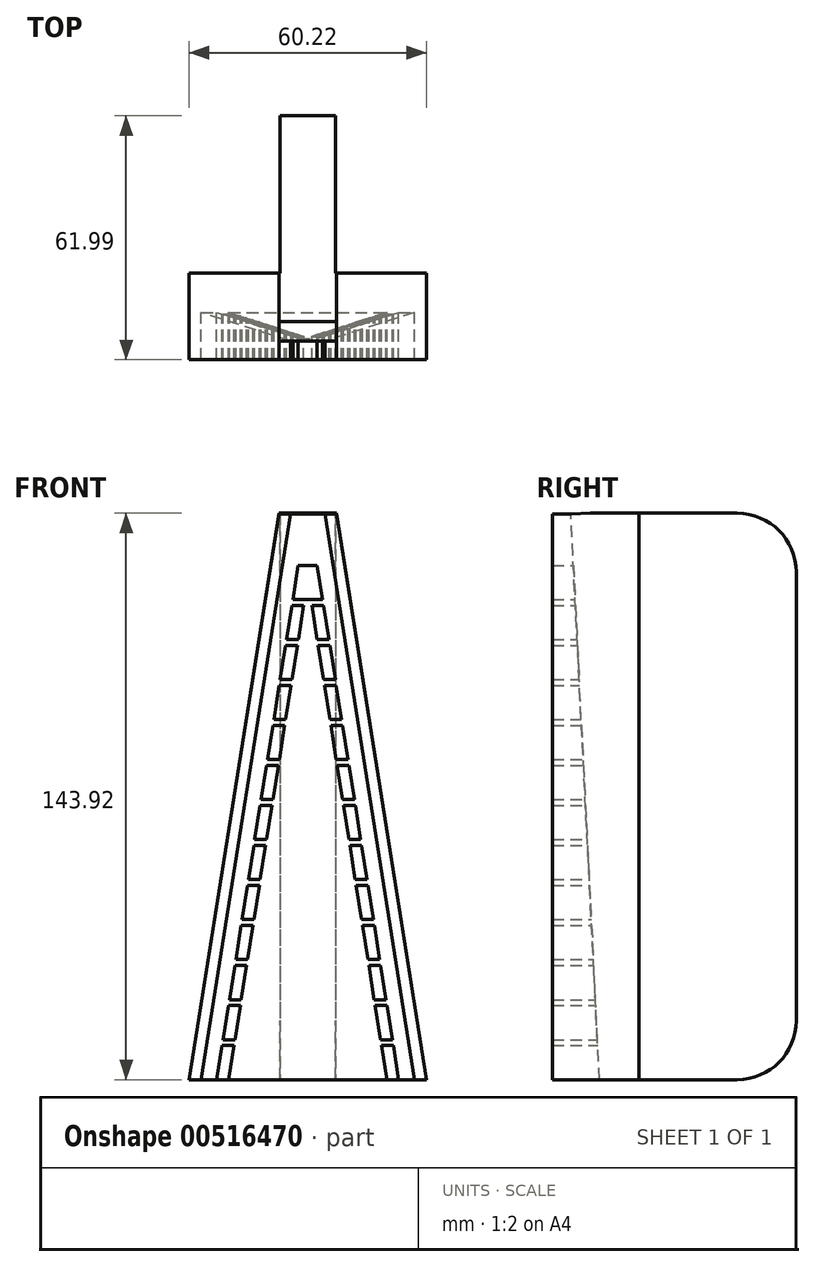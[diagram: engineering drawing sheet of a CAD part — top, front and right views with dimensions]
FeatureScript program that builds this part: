
annotation { "Feature Type Name" : "Feature", "Feature Type Description" : "" }
export const myFeature = defineFeature(function(context is Context, id is Id, definition is map)
    precondition{}
    {
        {
            var Q0;
            Q0=qCreatedBy(makeId("Front.planeOp"),FACE);
            var sketch = newSketch(context, id + "F0", { "sketchPlane" : qUnion([Q0])});
            skLineSegment(sketch, "E0", {"start": v(-21.74, 8.67) * mm, "end": v(-18.74, 8.67) * mm});
            skLineSegment(sketch, "E1", {"start": v(-18.74, 8.67) * mm, "end": v(-20.11, 0) * mm});
            skLineSegment(sketch, "E2", {"start": v(-20.11, 0) * mm, "end": v(-23.11, 0) * mm});
            skLineSegment(sketch, "E3", {"start": v(-23.11, 0) * mm, "end": v(-21.74, 8.67) * mm});
            skLineSegment(sketch, "E4", {"start": v(18.74, 8.67) * mm, "end": v(21.74, 8.67) * mm});
            skLineSegment(sketch, "E5", {"start": v(21.74, 8.67) * mm, "end": v(23.11, 0) * mm});
            skLineSegment(sketch, "E6", {"start": v(23.11, 0) * mm, "end": v(20.11, 0) * mm});
            skLineSegment(sketch, "E7", {"start": v(20.11, 0) * mm, "end": v(18.74, 8.67) * mm});
            skLineSegment(sketch, "E8", {"start": v(-21.5, 10.17) * mm, "end": v(-18.5, 10.17) * mm});
            skLineSegment(sketch, "E9", {"start": v(-18.5, 10.17) * mm, "end": v(-17.13, 18.83) * mm});
            skLineSegment(sketch, "E10", {"start": v(-17.13, 18.83) * mm, "end": v(-20.13, 18.83) * mm});
            skLineSegment(sketch, "E11", {"start": v(-20.13, 18.83) * mm, "end": v(-21.5, 10.17) * mm});
            skLineSegment(sketch, "E12", {"start": v(18.5, 10.17) * mm, "end": v(17.13, 18.83) * mm});
            skLineSegment(sketch, "E13", {"start": v(17.13, 18.83) * mm, "end": v(20.13, 18.83) * mm});
            skLineSegment(sketch, "E14", {"start": v(20.13, 18.83) * mm, "end": v(21.5, 10.17) * mm});
            skLineSegment(sketch, "E15", {"start": v(21.5, 10.17) * mm, "end": v(18.5, 10.17) * mm});
            skLineSegment(sketch, "E16", {"start": v(-18.52, 29) * mm, "end": v(-19.89, 20.33) * mm});
            skLineSegment(sketch, "E17", {"start": v(-19.89, 20.33) * mm, "end": v(-16.89, 20.33) * mm});
            skLineSegment(sketch, "E18", {"start": v(-16.89, 20.33) * mm, "end": v(-15.52, 29) * mm});
            skLineSegment(sketch, "E19", {"start": v(-15.52, 29) * mm, "end": v(-18.52, 29) * mm});
            skLineSegment(sketch, "E20", {"start": v(19.89, 20.33) * mm, "end": v(18.52, 29) * mm});
            skLineSegment(sketch, "E21", {"start": v(18.52, 29) * mm, "end": v(15.52, 29) * mm});
            skLineSegment(sketch, "E22", {"start": v(15.52, 29) * mm, "end": v(16.89, 20.33) * mm});
            skLineSegment(sketch, "E23", {"start": v(16.89, 20.33) * mm, "end": v(19.89, 20.33) * mm});
            skLineSegment(sketch, "E24", {"start": v(-16.67, 40.67) * mm, "end": v(-13.67, 40.67) * mm});
            skLineSegment(sketch, "E25", {"start": v(-13.67, 40.67) * mm, "end": v(-12.3, 49.33) * mm});
            skLineSegment(sketch, "E26", {"start": v(-12.3, 49.33) * mm, "end": v(-15.3, 49.33) * mm});
            skLineSegment(sketch, "E27", {"start": v(-15.3, 49.33) * mm, "end": v(-16.67, 40.67) * mm});
            skLineSegment(sketch, "E28", {"start": v(-13.69, 59.5) * mm, "end": v(-15.06, 50.83) * mm});
            skLineSegment(sketch, "E29", {"start": v(-8.84, 71.17) * mm, "end": v(-11.84, 71.17) * mm});
            skLineSegment(sketch, "E30", {"start": v(-7.47, 79.83) * mm, "end": v(-10.47, 79.83) * mm});
            skLineSegment(sketch, "E31", {"start": v(-10.47, 79.83) * mm, "end": v(-11.84, 71.17) * mm});
            skLineSegment(sketch, "E32", {"start": v(-8.86, 90) * mm, "end": v(-10.23, 81.33) * mm});
            skLineSegment(sketch, "E33", {"start": v(-10.23, 81.33) * mm, "end": v(-7.23, 81.33) * mm});
            skLineSegment(sketch, "E34", {"start": v(-7.23, 81.33) * mm, "end": v(-5.86, 90) * mm});
            skLineSegment(sketch, "E35", {"start": v(-5.86, 90) * mm, "end": v(-8.86, 90) * mm});
            skLineSegment(sketch, "E36", {"start": v(-7.25, 100.17) * mm, "end": v(-8.62, 91.5) * mm});
            skLineSegment(sketch, "E37", {"start": v(-8.62, 91.5) * mm, "end": v(-5.62, 91.5) * mm});
            skLineSegment(sketch, "E38", {"start": v(-5.62, 91.5) * mm, "end": v(-4.25, 100.17) * mm});
            skLineSegment(sketch, "E39", {"start": v(-7.25, 100.17) * mm, "end": v(-4.25, 100.17) * mm});
            skLineSegment(sketch, "E40", {"start": v(13.9, 39.17) * mm, "end": v(16.9, 39.17) * mm});
            skLineSegment(sketch, "E41", {"start": v(16.9, 39.17) * mm, "end": v(18.28, 30.5) * mm});
            skLineSegment(sketch, "E42", {"start": v(18.28, 30.5) * mm, "end": v(15.28, 30.5) * mm});
            skLineSegment(sketch, "E43", {"start": v(15.28, 30.5) * mm, "end": v(13.9, 39.17) * mm});
            skLineSegment(sketch, "E44", {"start": v(12.3, 49.33) * mm, "end": v(15.3, 49.33) * mm});
            skLineSegment(sketch, "E45", {"start": v(15.3, 49.33) * mm, "end": v(16.67, 40.67) * mm});
            skLineSegment(sketch, "E46", {"start": v(16.67, 40.67) * mm, "end": v(13.67, 40.67) * mm});
            skLineSegment(sketch, "E47", {"start": v(13.67, 40.67) * mm, "end": v(12.3, 49.33) * mm});
            skLineSegment(sketch, "E48", {"start": v(10.69, 59.5) * mm, "end": v(13.69, 59.5) * mm});
            skLineSegment(sketch, "E49", {"start": v(13.69, 59.5) * mm, "end": v(15.06, 50.83) * mm});
            skLineSegment(sketch, "E50", {"start": v(15.06, 50.83) * mm, "end": v(12.06, 50.83) * mm});
            skLineSegment(sketch, "E51", {"start": v(12.06, 50.83) * mm, "end": v(10.69, 59.5) * mm});
            skLineSegment(sketch, "E52", {"start": v(13.45, 61) * mm, "end": v(10.45, 61) * mm});
            skLineSegment(sketch, "E53", {"start": v(7.47, 79.83) * mm, "end": v(10.47, 79.83) * mm});
            skLineSegment(sketch, "E54", {"start": v(10.47, 79.83) * mm, "end": v(11.84, 71.17) * mm});
            skLineSegment(sketch, "E55", {"start": v(11.84, 71.17) * mm, "end": v(8.84, 71.17) * mm});
            skLineSegment(sketch, "E56", {"start": v(8.84, 71.17) * mm, "end": v(7.47, 79.83) * mm});
            skLineSegment(sketch, "E57", {"start": v(5.86, 90) * mm, "end": v(8.86, 90) * mm});
            skLineSegment(sketch, "E58", {"start": v(8.86, 90) * mm, "end": v(10.23, 81.33) * mm});
            skLineSegment(sketch, "E59", {"start": v(10.23, 81.33) * mm, "end": v(7.23, 81.33) * mm});
            skLineSegment(sketch, "E60", {"start": v(7.23, 81.33) * mm, "end": v(5.86, 90) * mm});
            skLineSegment(sketch, "E61", {"start": v(-23.11, 192.36) * mm, "end": v(-23.11, -60.17) * mm, "construction": true});
            skLineSegment(sketch, "E62", {"start": v(-16.9, 39.17) * mm, "end": v(-18.28, 30.5) * mm});
            skLineSegment(sketch, "E63", {"start": v(-18.28, 30.5) * mm, "end": v(-15.28, 30.5) * mm});
            skLineSegment(sketch, "E64", {"start": v(-15.28, 30.5) * mm, "end": v(-13.9, 39.17) * mm});
            skLineSegment(sketch, "E65", {"start": v(-13.9, 39.17) * mm, "end": v(-16.9, 39.17) * mm});
            skLineSegment(sketch, "E66", {"start": v(23.11, 282.2) * mm, "end": v(23.11, 74.17) * mm, "construction": true});
            skLineSegment(sketch, "E67", {"start": v(-18.5, 10.17) * mm, "end": v(18.5, 10.17) * mm, "construction": true});
            skLineSegment(sketch, "E68", {"start": v(-20.11, 0) * mm, "end": v(20.11, 0) * mm, "construction": true});
            skLineSegment(sketch, "E69", {"start": v(-18.74, 8.67) * mm, "end": v(18.74, 8.67) * mm, "construction": true});
            skLineSegment(sketch, "E70", {"start": v(-17.13, 18.83) * mm, "end": v(17.13, 18.83) * mm, "construction": true});
            skLineSegment(sketch, "E71", {"start": v(-16.89, 20.33) * mm, "end": v(16.89, 20.33) * mm, "construction": true});
            skLineSegment(sketch, "E72", {"start": v(-15.52, 29) * mm, "end": v(15.52, 29) * mm, "construction": true});
            skLineSegment(sketch, "E73", {"start": v(-15.28, 30.5) * mm, "end": v(15.28, 30.5) * mm, "construction": true});
            skLineSegment(sketch, "E74", {"start": v(-13.9, 39.17) * mm, "end": v(13.9, 39.17) * mm, "construction": true});
            skLineSegment(sketch, "E75", {"start": v(-13.67, 40.67) * mm, "end": v(13.67, 40.67) * mm, "construction": true});
            skLineSegment(sketch, "E76", {"start": v(-12.3, 49.33) * mm, "end": v(12.3, 49.33) * mm, "construction": true});
            skLineSegment(sketch, "E77", {"start": v(-7.47, 79.83) * mm, "end": v(7.47, 79.83) * mm, "construction": true});
            skLineSegment(sketch, "E78", {"start": v(-7.23, 81.33) * mm, "end": v(7.23, 81.33) * mm, "construction": true});
            skLineSegment(sketch, "E79", {"start": v(-5.86, 90) * mm, "end": v(5.86, 90) * mm, "construction": true});
            skLineSegment(sketch, "E80", {"start": v(-5.62, 91.5) * mm, "end": v(5.62, 91.5) * mm, "construction": true});
            skLineSegment(sketch, "E81", {"start": v(-4.25, 100.17) * mm, "end": v(4.25, 100.17) * mm, "construction": true});
            skLineSegment(sketch, "E82", {"start": v(-21.74, 8.67) * mm, "end": v(-21.5, 10.17) * mm, "construction": true});
            skLineSegment(sketch, "E83", {"start": v(-20.13, 18.83) * mm, "end": v(-19.89, 20.33) * mm, "construction": true});
            skLineSegment(sketch, "E84", {"start": v(-18.52, 29) * mm, "end": v(-18.28, 30.5) * mm, "construction": true});
            skLineSegment(sketch, "E85", {"start": v(-16.9, 39.17) * mm, "end": v(-16.67, 40.67) * mm, "construction": true});
            skLineSegment(sketch, "E86", {"start": v(-15.3, 49.33) * mm, "end": v(-15.06, 50.83) * mm, "construction": true});
            skLineSegment(sketch, "E87", {"start": v(-13.69, 59.5) * mm, "end": v(-13.45, 61) * mm, "construction": true});
            skLineSegment(sketch, "E88", {"start": v(-11.84, 71.17) * mm, "end": v(-11.84, 71.17) * mm});
            skLineSegment(sketch, "E89", {"start": v(-10.23, 81.33) * mm, "end": v(-10.47, 79.83) * mm, "construction": true});
            skLineSegment(sketch, "E90", {"start": v(-8.86, 90) * mm, "end": v(-8.62, 91.5) * mm, "construction": true});
            skLineSegment(sketch, "E91", {"start": v(-13.69, 59.5) * mm, "end": v(-10.69, 59.5) * mm});
            skLineSegment(sketch, "E92", {"start": v(-10.69, 59.5) * mm, "end": v(-12.06, 50.83) * mm});
            skLineSegment(sketch, "E93", {"start": v(-12.06, 50.83) * mm, "end": v(-15.06, 50.83) * mm});
            skLineSegment(sketch, "E94", {"start": v(-10.69, 59.5) * mm, "end": v(10.69, 59.5) * mm, "construction": true});
            skLineSegment(sketch, "E95", {"start": v(-12.06, 50.83) * mm, "end": v(12.06, 50.83) * mm, "construction": true});
            skLineSegment(sketch, "E96", {"start": v(-18.74, 8.67) * mm, "end": v(-18.5, 10.17) * mm, "construction": true});
            skLineSegment(sketch, "E97", {"start": v(-17.13, 18.83) * mm, "end": v(-16.89, 20.33) * mm, "construction": true});
            skLineSegment(sketch, "E98", {"start": v(-15.52, 29) * mm, "end": v(-15.28, 30.5) * mm, "construction": true});
            skLineSegment(sketch, "E99", {"start": v(-13.9, 39.17) * mm, "end": v(-13.67, 40.67) * mm, "construction": true});
            skLineSegment(sketch, "E100", {"start": v(-12.3, 49.33) * mm, "end": v(-12.06, 50.83) * mm, "construction": true});
            skLineSegment(sketch, "E101", {"start": v(-8.84, 71.17) * mm, "end": v(8.84, 71.17) * mm, "construction": true});
            skLineSegment(sketch, "E102", {"start": v(-13.45, 61) * mm, "end": v(-12.08, 69.67) * mm});
            skLineSegment(sketch, "E103", {"start": v(13.45, 61) * mm, "end": v(12.08, 69.67) * mm});
            skLineSegment(sketch, "E104", {"start": v(12.08, 69.67) * mm, "end": v(9.08, 69.67) * mm});
            skLineSegment(sketch, "E105", {"start": v(9.08, 69.67) * mm, "end": v(10.45, 61) * mm});
            skLineSegment(sketch, "E106", {"start": v(-7.47, 79.83) * mm, "end": v(-7.23, 81.33) * mm, "construction": true});
            skLineSegment(sketch, "E107", {"start": v(-5.86, 90) * mm, "end": v(-5.62, 91.5) * mm, "construction": true});
            skLineSegment(sketch, "E108", {"start": v(-12.08, 69.67) * mm, "end": v(-9.08, 69.67) * mm});
            skLineSegment(sketch, "E109", {"start": v(-9.08, 69.67) * mm, "end": v(-10.45, 61) * mm});
            skLineSegment(sketch, "E110", {"start": v(-10.45, 61) * mm, "end": v(-13.45, 61) * mm});
            skLineSegment(sketch, "E111", {"start": v(-12.08, 69.67) * mm, "end": v(-11.84, 71.17) * mm, "construction": true});
            skLineSegment(sketch, "E112", {"start": v(-8.84, 71.17) * mm, "end": v(-9.08, 69.67) * mm, "construction": true});
            skLineSegment(sketch, "E113", {"start": v(-10.45, 61) * mm, "end": v(-10.69, 59.5) * mm, "construction": true});
            skLineSegment(sketch, "E114", {"start": v(-7.47, 79.83) * mm, "end": v(-8.84, 71.17) * mm});
            skLineSegment(sketch, "E115", {"start": v(-9.08, 69.67) * mm, "end": v(9.08, 69.67) * mm, "construction": true});
            skLineSegment(sketch, "E116", {"start": v(-10.45, 61) * mm, "end": v(10.45, 61) * mm, "construction": true});
            skLineSegment(sketch, "E117", {"start": v(15.52, 29) * mm, "end": v(15.28, 30.5) * mm, "construction": true});
            skLineSegment(sketch, "E118", {"start": v(18.28, 30.5) * mm, "end": v(18.52, 29) * mm, "construction": true});
            skLineSegment(sketch, "E119", {"start": v(16.67, 40.67) * mm, "end": v(16.9, 39.17) * mm, "construction": true});
            skLineSegment(sketch, "E120", {"start": v(13.67, 40.67) * mm, "end": v(13.9, 39.17) * mm, "construction": true});
            skLineSegment(sketch, "E121", {"start": v(20.13, 18.83) * mm, "end": v(19.89, 20.33) * mm, "construction": true});
            skLineSegment(sketch, "E122", {"start": v(17.13, 18.83) * mm, "end": v(16.89, 20.33) * mm, "construction": true});
            skLineSegment(sketch, "E123", {"start": v(10.23, 81.33) * mm, "end": v(10.47, 79.83) * mm, "construction": true});
            skLineSegment(sketch, "E124", {"start": v(12.08, 69.67) * mm, "end": v(11.84, 71.17) * mm, "construction": true});
            skLineSegment(sketch, "E125", {"start": v(13.45, 61) * mm, "end": v(13.69, 59.5) * mm, "construction": true});
            skLineSegment(sketch, "E126", {"start": v(10.69, 59.5) * mm, "end": v(10.45, 61) * mm, "construction": true});
            skLineSegment(sketch, "E127", {"start": v(9.08, 69.67) * mm, "end": v(8.84, 71.17) * mm, "construction": true});
            skLineSegment(sketch, "E128", {"start": v(7.47, 79.83) * mm, "end": v(7.23, 81.33) * mm, "construction": true});
            skLineSegment(sketch, "E129", {"start": v(5.86, 90) * mm, "end": v(5.62, 91.5) * mm, "construction": true});
            skLineSegment(sketch, "E130", {"start": v(12.06, 50.83) * mm, "end": v(12.3, 49.33) * mm, "construction": true});
            skLineSegment(sketch, "E131", {"start": v(15.3, 49.33) * mm, "end": v(15.06, 50.83) * mm, "construction": true});
            skLineSegment(sketch, "E132", {"start": v(18.5, 10.17) * mm, "end": v(18.74, 8.67) * mm, "construction": true});
            skLineSegment(sketch, "E133", {"start": v(21.5, 10.17) * mm, "end": v(21.74, 8.67) * mm, "construction": true});
            skLineSegment(sketch, "E134", {"start": v(4.25, 100.17) * mm, "end": v(5.62, 91.5) * mm});
            skLineSegment(sketch, "E135", {"start": v(5.62, 91.5) * mm, "end": v(8.62, 91.5) * mm});
            skLineSegment(sketch, "E136", {"start": v(8.62, 91.5) * mm, "end": v(7.25, 100.17) * mm});
            skLineSegment(sketch, "E137", {"start": v(7.25, 100.17) * mm, "end": v(4.25, 100.17) * mm});
            skLineSegment(sketch, "E138", {"start": v(8.62, 91.5) * mm, "end": v(8.86, 90) * mm, "construction": true});
            skLineSegment(sketch, "E139", {"start": v(27.82, 100.17) * mm, "end": v(27.82, 91.5) * mm, "construction": true});
            skLineSegment(sketch, "E140", {"start": v(16.69, 90) * mm, "end": v(16.69, 81.33) * mm, "construction": true});
            skLineSegment(sketch, "E141", {"start": v(15.77, 79.83) * mm, "end": v(15.77, 71.17) * mm, "construction": true});
            skLineSegment(sketch, "E142", {"start": v(14.86, 69.67) * mm, "end": v(14.86, 61) * mm, "construction": true});
            skLineSegment(sketch, "E143", {"start": v(10.43, 59.5) * mm, "end": v(10.43, 50.83) * mm, "construction": true});
            skLineSegment(sketch, "E144", {"start": v(9.82, 49.33) * mm, "end": v(9.82, 40.67) * mm, "construction": true});
            skLineSegment(sketch, "E145", {"start": v(9.06, 39.17) * mm, "end": v(9.06, 30.5) * mm, "construction": true});
            skLineSegment(sketch, "E146", {"start": v(7.38, 29) * mm, "end": v(7.38, 20.33) * mm, "construction": true});
            skLineSegment(sketch, "E147", {"start": v(9.21, 18.83) * mm, "end": v(9.21, 10.17) * mm, "construction": true});
            skLineSegment(sketch, "E148", {"start": v(-201.28, 8.67) * mm, "end": v(-201.28, 0) * mm, "construction": true});
            skLineSegment(sketch, "E149", {"start": v(104.46, 8.67) * mm, "end": v(104.46, 10.17) * mm, "construction": true});
            skLineSegment(sketch, "E150", {"start": v(102.28, 18.83) * mm, "end": v(102.28, 20.33) * mm, "construction": true});
            skLineSegment(sketch, "E151", {"start": v(106.09, 29) * mm, "end": v(106.09, 30.5) * mm, "construction": true});
            skLineSegment(sketch, "E152", {"start": v(98.47, 39.17) * mm, "end": v(98.47, 40.67) * mm, "construction": true});
            skLineSegment(sketch, "E153", {"start": v(104.46, 49.33) * mm, "end": v(104.46, 50.83) * mm, "construction": true});
            skLineSegment(sketch, "E154", {"start": v(94.3, 59.5) * mm, "end": v(94.3, 61) * mm, "construction": true});
            skLineSegment(sketch, "E155", {"start": v(102.64, 69.67) * mm, "end": v(102.64, 71.17) * mm, "construction": true});
            skLineSegment(sketch, "E156", {"start": v(87.4, 79.83) * mm, "end": v(87.4, 81.33) * mm, "construction": true});
            skLineSegment(sketch, "E157", {"start": v(98.1, 90) * mm, "end": v(98.1, 91.5) * mm, "construction": true});
            skLineSegment(sketch, "E158", {"start": v(-6.41, 130.67) * mm, "end": v(-27.11, 0) * mm});
            skLineSegment(sketch, "E159", {"start": v(-27.11, 0) * mm, "end": v(-30.11, 0) * mm});
            skLineSegment(sketch, "E160", {"start": v(-30.11, 0) * mm, "end": v(-9.41, 130.67) * mm});
            skLineSegment(sketch, "E161", {"start": v(-9.41, 130.67) * mm, "end": v(-6.41, 130.67) * mm});
            skLineSegment(sketch, "E162", {"start": v(6.41, 130.67) * mm, "end": v(9.41, 130.67) * mm});
            skLineSegment(sketch, "E163", {"start": v(9.41, 130.67) * mm, "end": v(30.11, 0) * mm});
            skLineSegment(sketch, "E164", {"start": v(30.11, 0) * mm, "end": v(27.11, 0) * mm});
            skLineSegment(sketch, "E165", {"start": v(27.11, 0) * mm, "end": v(6.41, 130.67) * mm});
            skLineSegment(sketch, "E166", {"start": v(-27.11, 0) * mm, "end": v(-23.11, 0) * mm, "construction": true});
            skLineSegment(sketch, "E167", {"start": v(23.11, 0) * mm, "end": v(27.11, 0) * mm, "construction": true});
            skLineSegment(sketch, "E168", {"start": v(-7, 101.67) * mm, "end": v(-4, 101.67) * mm});
            skLineSegment(sketch, "E169", {"start": v(-4, 101.67) * mm, "end": v(-2.64, 110.33) * mm});
            skLineSegment(sketch, "E170", {"start": v(-2.64, 110.33) * mm, "end": v(-5.64, 110.33) * mm});
            skLineSegment(sketch, "E171", {"start": v(-5.64, 110.33) * mm, "end": v(-7, 101.67) * mm});
            skLineSegment(sketch, "E172", {"start": v(2.64, 110.33) * mm, "end": v(5.64, 110.33) * mm});
            skLineSegment(sketch, "E173", {"start": v(5.64, 110.33) * mm, "end": v(7, 101.67) * mm});
            skLineSegment(sketch, "E174", {"start": v(7, 101.67) * mm, "end": v(4, 101.67) * mm});
            skLineSegment(sketch, "E175", {"start": v(4, 101.67) * mm, "end": v(2.64, 110.33) * mm});
            skLineSegment(sketch, "E176", {"start": v(-4, 101.67) * mm, "end": v(4, 101.67) * mm, "construction": true});
            skLineSegment(sketch, "E177", {"start": v(-2.64, 110.33) * mm, "end": v(2.64, 110.33) * mm, "construction": true});
            skLineSegment(sketch, "E178", {"start": v(0, 110.33) * mm, "end": v(0, 101.67) * mm, "construction": true});
            skLineSegment(sketch, "E179", {"start": v(0.52, 101.67) * mm, "end": v(0.52, 100.17) * mm, "construction": true});
            skLineSegment(sketch, "E180", {"start": v(-7.25, 100.17) * mm, "end": v(-7, 101.67) * mm, "construction": true});
            skLineSegment(sketch, "E181", {"start": v(7, 101.67) * mm, "end": v(7.25, 100.17) * mm, "construction": true});
            skLineSegment(sketch, "E182", {"start": v(4.25, 100.17) * mm, "end": v(4, 101.67) * mm, "construction": true});
            skLineSegment(sketch, "E183", {"start": v(-5.4, 111.83) * mm, "end": v(-2.4, 111.83) * mm});
            skLineSegment(sketch, "E184", {"start": v(-2.4, 111.83) * mm, "end": v(-1.02, 120.5) * mm});
            skLineSegment(sketch, "E185", {"start": v(-1.02, 120.5) * mm, "end": v(-4.02, 120.5) * mm});
            skLineSegment(sketch, "E186", {"start": v(-4.02, 120.5) * mm, "end": v(-5.4, 111.83) * mm});
            skLineSegment(sketch, "E187", {"start": v(1.02, 120.5) * mm, "end": v(4.02, 120.5) * mm});
            skLineSegment(sketch, "E188", {"start": v(4.02, 120.5) * mm, "end": v(5.4, 111.83) * mm});
            skLineSegment(sketch, "E189", {"start": v(5.4, 111.83) * mm, "end": v(2.4, 111.83) * mm});
            skLineSegment(sketch, "E190", {"start": v(2.4, 111.83) * mm, "end": v(1.02, 120.5) * mm});
            skLineSegment(sketch, "E191", {"start": v(-2.4, 111.83) * mm, "end": v(2.4, 111.83) * mm, "construction": true});
            skLineSegment(sketch, "E192", {"start": v(-1.02, 120.5) * mm, "end": v(1.02, 120.5) * mm, "construction": true});
            skLineSegment(sketch, "E193", {"start": v(0, 120.5) * mm, "end": v(0, 111.83) * mm, "construction": true});
            skLineSegment(sketch, "E194", {"start": v(5.4, 111.83) * mm, "end": v(5.64, 110.33) * mm, "construction": true});
            skLineSegment(sketch, "E195", {"start": v(0.6, 111.83) * mm, "end": v(0.6, 110.33) * mm, "construction": true});
            skLineSegment(sketch, "E196", {"start": v(2.64, 110.33) * mm, "end": v(2.4, 111.83) * mm, "construction": true});
            skLineSegment(sketch, "E197", {"start": v(-2.64, 110.33) * mm, "end": v(-2.4, 111.83) * mm, "construction": true});
            skLineSegment(sketch, "E198", {"start": v(-5.64, 110.33) * mm, "end": v(-5.4, 111.83) * mm, "construction": true});
            skLineSegment(sketch, "E199", {"start": v(-2.41, 130.67) * mm, "end": v(-3.79, 122) * mm});
            skLineSegment(sketch, "E200", {"start": v(2.41, 130.67) * mm, "end": v(3.79, 122) * mm});
            skLineSegment(sketch, "E201", {"start": v(4.02, 120.5) * mm, "end": v(3.79, 122) * mm, "construction": true});
            skLineSegment(sketch, "E202", {"start": v(-4.02, 120.5) * mm, "end": v(-3.79, 122) * mm, "construction": true});
            skLineSegment(sketch, "E203", {"start": v(-3.79, 122) * mm, "end": v(3.79, 122) * mm});
            skLineSegment(sketch, "E204", {"start": v(-2.41, 130.67) * mm, "end": v(2.41, 130.67) * mm});
            skLineSegment(sketch, "E205", {"start": v(0, 130.67) * mm, "end": v(0, 122) * mm, "construction": true});
            skLineSegment(sketch, "E206", {"start": v(0.43, 122) * mm, "end": v(0.43, 120.5) * mm, "construction": true});
            skLineSegment(sketch, "E207", {"start": v(-6.41, 130.67) * mm, "end": v(-2.41, 130.67) * mm, "construction": true});
            skLineSegment(sketch, "E208", {"start": v(6.41, 130.67) * mm, "end": v(2.41, 130.67) * mm, "construction": true});
            skLineSegment(sketch, "E209", {"start": v(-9.41, 130.67) * mm, "end": v(-7.36, 143.67) * mm});
            skLineSegment(sketch, "E210", {"start": v(-7.36, 143.67) * mm, "end": v(-4.36, 143.67) * mm});
            skLineSegment(sketch, "E211", {"start": v(-4.36, 143.67) * mm, "end": v(-6.41, 130.67) * mm});
            skLineSegment(sketch, "E212", {"start": v(6.41, 130.67) * mm, "end": v(4.36, 143.67) * mm});
            skLineSegment(sketch, "E213", {"start": v(4.36, 143.67) * mm, "end": v(7.36, 143.67) * mm});
            skLineSegment(sketch, "E214", {"start": v(7.36, 143.67) * mm, "end": v(9.41, 130.67) * mm});
            skLineSegment(sketch, "E215", {"start": v(-4.36, 143.67) * mm, "end": v(4.36, 143.67) * mm, "construction": true});
            skSolve(sketch);
        }
        {
            var Q0;
            Q0=qSketchRegion(id+"F0",true);
            extrude(context, id + "F1", {"entities" : qUnion([Q0]), "depth" : 12 * mm, "offsetDistance" : 25 * mm});
        }
        {
            var Q0;
            Q0=qCreatedBy(makeId("Right.planeOp"),FACE);
            var sketch = newSketch(context, id + "F2", { "sketchPlane" : qUnion([Q0])});
            skLineSegment(sketch, "E216", {"start": v(0, 0) * mm, "end": v(-7.28, 143.67) * mm});
            skLineSegment(sketch, "E217", {"start": v(-7.28, 143.67) * mm, "end": v(0, 143.67) * mm});
            skLineSegment(sketch, "E218", {"start": v(0, 143.67) * mm, "end": v(0, 0) * mm});
            skSolve(sketch);
        }
        {
            var Q0;
            Q0=qSketchRegion(id+"F2",true);
            extrude(context, id + "F3", {"entities" : qUnion([Q0]), "operationType" : NewBodyOperationType.REMOVE, "depth" : 80 * mm, "offsetDistance" : 25 * mm, "symmetric" : true});
        }
        {
            var Q0;
            Q0=makeQuery(id+"F3.boolean.opBoolean","COPY",FACE,{"disambiguationData":[TD([makeQuery(id+"F1.opExtrude","SWEPT_FACE",FACE,{"disambiguationData":[OSD([sQuery(id+"F0.wireOp",EDGE,"E164")])]})])],"derivedFrom":makeQuery(id+"F3.opExtrude","SWEPT_FACE",FACE,{"disambiguationData":[OSD([sQuery(id+"F2.wireOp",EDGE,"E216")])]})});
            var sketch = newSketch(context, id + "F4", { "sketchPlane" : qUnion([Q0])});
            skLineSegment(sketch, "E219", {"start": v(-7.36, 143.85) * mm, "end": v(7.36, 143.85) * mm});
            skLineSegment(sketch, "E220", {"start": v(7.36, 143.85) * mm, "end": v(30.11, 0) * mm});
            skLineSegment(sketch, "E221", {"start": v(30.11, 0) * mm, "end": v(-30.11, 0) * mm});
            skLineSegment(sketch, "E222", {"start": v(-30.11, 0) * mm, "end": v(-7.36, 143.85) * mm});
            skSolve(sketch);
        }
        {
            var Q0;
            Q0=qSketchRegion(id+"F4",true);
            extrude(context, id + "F5", {"entities" : qUnion([Q0]), "operationType" : NewBodyOperationType.ADD, "depth" : 5 * mm, "offsetDistance" : 25 * mm});
        }
        {
            var Q0;
            Q0=qCreatedBy(makeId("Right.planeOp"),FACE);
            var sketch = newSketch(context, id + "F6", { "sketchPlane" : qUnion([Q0])});
            skLineSegment(sketch, "E223", {"start": v(-2.28, 143.92) * mm, "end": v(5, 0.25) * mm});
            skLineSegment(sketch, "E224", {"start": v(5, 0.25) * mm, "end": v(10, 0.25) * mm});
            skLineSegment(sketch, "E225", {"start": v(10, 0.25) * mm, "end": v(10, 143.92) * mm});
            skLineSegment(sketch, "E226", {"start": v(10, 143.92) * mm, "end": v(-2.28, 143.92) * mm});
            skSolve(sketch);
        }
        {
            var Q0;
            Q0=qSketchRegion(id+"F6",true);
            extrude(context, id + "F7", {"entities" : qUnion([Q0]), "operationType" : NewBodyOperationType.ADD, "depth" : 62 * mm, "offsetDistance" : 25 * mm, "symmetric" : true});
        }
        {
            var Q0;
            Q0=qCreatedBy(makeId("Right.planeOp"),FACE);
            var sketch = newSketch(context, id + "F8", { "sketchPlane" : qUnion([Q0])});
            skLineSegment(sketch, "E227", {"start": v(5, 0.25) * mm, "end": v(0, 0) * mm});
            skLineSegment(sketch, "E228", {"start": v(0, 0) * mm, "end": v(10, 0) * mm});
            skLineSegment(sketch, "E229", {"start": v(10, 0) * mm, "end": v(10, 0.25) * mm});
            skLineSegment(sketch, "E230", {"start": v(10, 0.25) * mm, "end": v(5, 0.25) * mm});
            skSolve(sketch);
        }
        {
            var Q0;
            Q0=qSketchRegion(id+"F8",true);
            extrude(context, id + "F9", {"entities" : qUnion([Q0]), "operationType" : NewBodyOperationType.ADD, "depth" : 63 * mm, "offsetDistance" : 25 * mm, "symmetric" : true});
        }
        {
            var Q0;
            Q0=qCreatedBy(makeId("Front.planeOp"),FACE);
            var sketch = newSketch(context, id + "F10", { "sketchPlane" : qUnion([Q0])});
            skLineSegment(sketch, "E231", {"start": v(31, 143.92) * mm, "end": v(31.5, 0) * mm});
            skLineSegment(sketch, "E232", {"start": v(31.5, 0) * mm, "end": v(30.11, 0) * mm});
            skLineSegment(sketch, "E233", {"start": v(30.11, 0) * mm, "end": v(7.36, 143.92) * mm});
            skLineSegment(sketch, "E234", {"start": v(7.36, 143.92) * mm, "end": v(31, 143.92) * mm});
            skLineSegment(sketch, "E235", {"start": v(-7.36, 143.92) * mm, "end": v(-30.11, 0) * mm});
            skLineSegment(sketch, "E236", {"start": v(-30.11, 0) * mm, "end": v(-31.5, 0) * mm});
            skLineSegment(sketch, "E237", {"start": v(-31.5, 0) * mm, "end": v(-31, 143.92) * mm});
            skLineSegment(sketch, "E238", {"start": v(-31, 143.92) * mm, "end": v(-7.36, 143.92) * mm});
            skSolve(sketch);
        }
        {
            var Q0;
            Q0=qSketchRegion(id+"F10",true);
            extrude(context, id + "F11", {"entities" : qUnion([Q0]), "operationType" : NewBodyOperationType.REMOVE, "depth" : 30 * mm, "offsetDistance" : 25 * mm, "symmetric" : true});
        }
        {
            var Q0;
            Q0=qCreatedBy(makeId("Right.planeOp"),FACE);
            var sketch = newSketch(context, id + "F12", { "sketchPlane" : qUnion([Q0])});
            skLineSegment(sketch, "E239.bottom", {"start": v(50, 143.92) * mm, "end": v(10, 143.92) * mm});
            skLineSegment(sketch, "E239.top", {"start": v(50, 0) * mm, "end": v(10, 0) * mm});
            skLineSegment(sketch, "E239.left", {"start": v(50, 143.92) * mm, "end": v(50, 0) * mm});
            skLineSegment(sketch, "E239.right", {"start": v(10, 143.92) * mm, "end": v(10, 0) * mm});
            skSolve(sketch);
        }
        {
            var Q0;
            Q0 = qSketchRegion(id + "F12", true);
            extrude(context, id + "F13", {"entities" : qUnion([Q0]), "operationType" : NewBodyOperationType.ADD, "depth" : 14 * mm, "offsetDistance" : 25 * mm, "symmetric" : true});
        }
        {
            var Q0;
            Q0=makeQuery(id+"F13.opExtrude","SWEPT_EDGE",EDGE,{"disambiguationData":[OSD([sQuery(id+"F12.wireOp",EDGE,"E239.bottom"),sQuery(id+"F12.wireOp",EDGE,"E239.left")])]});
            var Q1;
            Q1=makeQuery(id+"F13.opExtrude","SWEPT_EDGE",EDGE,{"disambiguationData":[OSD([sQuery(id+"F12.wireOp",EDGE,"E239.top"),sQuery(id+"F12.wireOp",EDGE,"E239.left")])]});
            fillet(context, id + "F14", {"entities" : qUnion([Q0, Q1]), "radius" : 15 * mm, "tangentPropagation" : true, "allowEdgeOverflow" : false});
        }
    });
